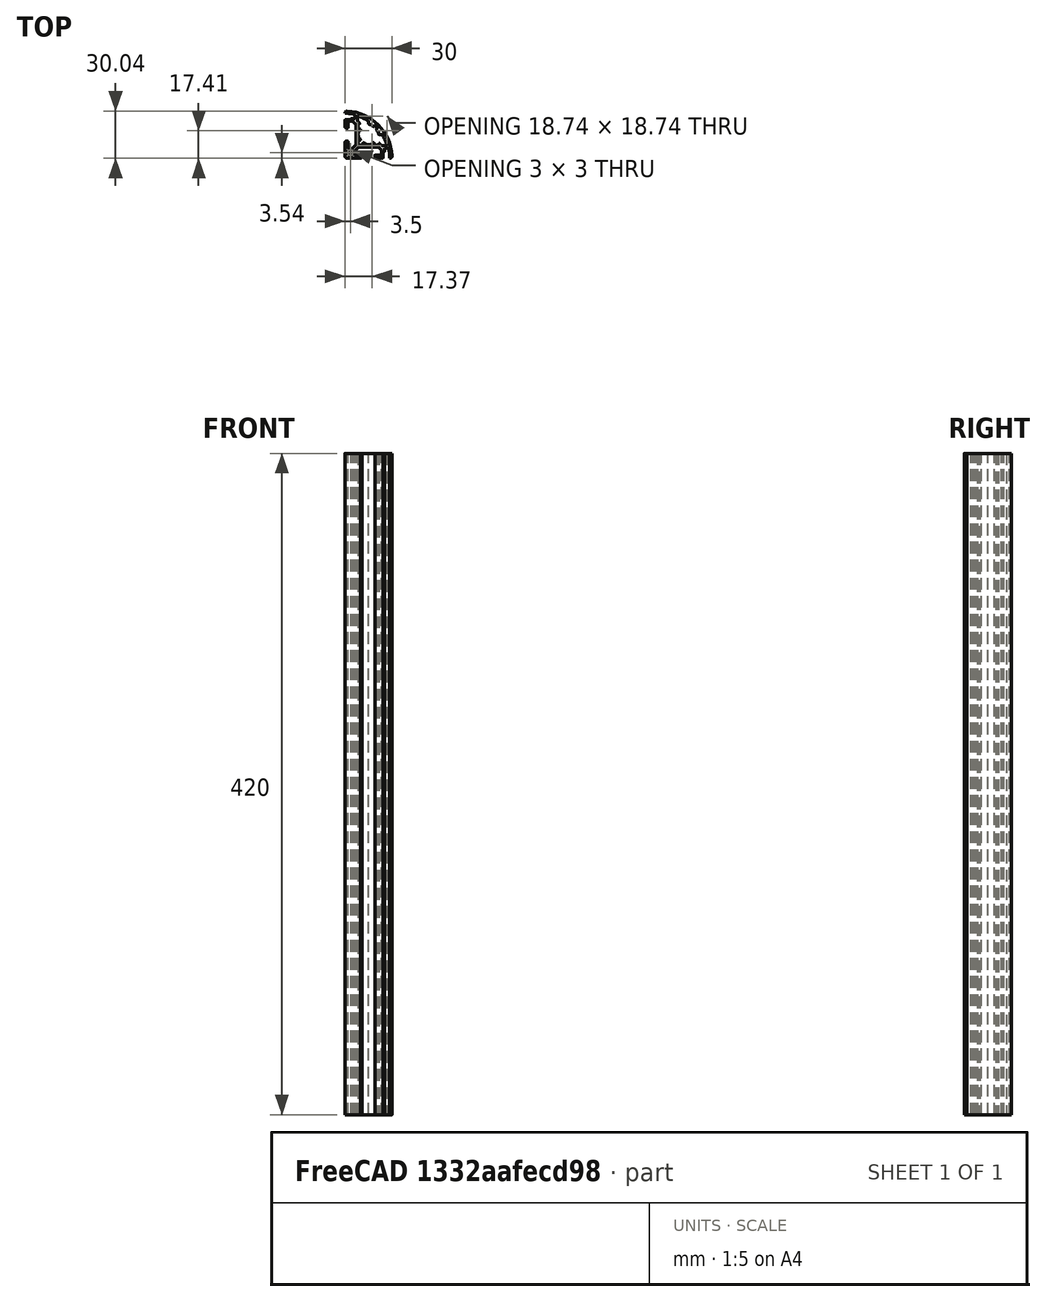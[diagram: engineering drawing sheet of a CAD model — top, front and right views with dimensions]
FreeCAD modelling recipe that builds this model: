
FCSTD DOCUMENT  (FreeCAD 0.17R13387 (Git))
Label: Z-Profile_3030_rounded_enclosure
License: All rights reserved
LicenseURL: http://en.wikipedia.org/wiki/All_rights_reserved
objects: Sketcher::SketchObject×1, PartDesign::Pad×1, PartDesign::Body×1
note: 4 computed .brp shape members not serialized (recipe doc carries the construction recipe); baked Part::Feature solids carry a one-line shape summary decoded from their .brp

FEATURE [Sketcher::SketchObject] Sketch155
  sketch-geometry (152):
    g0: ArcOfCircle CenterX=4.7 CenterY=4.69999 CenterZ=0 NormalX=0 NormalY=0 NormalZ=1 AngleXU=0 Radius=0.3 StartAngle=0 EndAngle=1.5708
    g1: ArcOfCircle CenterX=8.81823 CenterY=16.657 CenterZ=0 NormalX=0 NormalY=0 NormalZ=1 AngleXU=0 Radius=0.1 StartAngle=1.7017 EndAngle=2.8797
    g2: ArcOfCircle CenterX=15 CenterY=15 CenterZ=0 NormalX=0 NormalY=0 NormalZ=1 AngleXU=0 Radius=6.5 StartAngle=3.14159 EndAngle=3.40349
    g3: LineSegment StartX=8.80518 StartY=13.2438 StartZ=0 EndX=9.16477 EndY=13.1965 EndZ=0
    g4: ArcOfCircle CenterX=8.81823 CenterY=13.343 CenterZ=0 NormalX=0 NormalY=0 NormalZ=1 AngleXU=0 Radius=0.1 StartAngle=3.40349 EndAngle=4.58149
    g5: ArcOfCircle CenterX=15 CenterY=15 CenterZ=0 NormalX=0 NormalY=0 NormalZ=1 AngleXU=0 Radius=6.5 StartAngle=2.8797 EndAngle=3.14159
    g6: ArcOfCircle CenterX=9.15172 CenterY=13.0973 CenterZ=0 NormalX=0 NormalY=0 NormalZ=1 AngleXU=3.14159 Radius=0.1 StartAngle=3.45613 EndAngle=4.58149
    g7: ArcOfCircle CenterX=15 CenterY=15 CenterZ=0 NormalX=0 NormalY=0 NormalZ=1 AngleXU=0 Radius=6.05 StartAngle=3.45613 EndAngle=3.68754
    g8: ArcOfCircle CenterX=9.57305 CenterY=11.7029 CenterZ=0 NormalX=0 NormalY=0 NormalZ=1 AngleXU=3.14159 Radius=0.3 StartAngle=2.00713 EndAngle=3.68754
    g9: LineSegment StartX=9.69983 StartY=11.431 StartZ=0 EndX=8.60619 EndY=10.921 EndZ=0
    g10: ArcOfCircle CenterX=8.73298 CenterY=10.6492 CenterZ=0 NormalX=0 NormalY=0 NormalZ=1 AngleXU=0 Radius=0.3 StartAngle=2.00713 EndAngle=3.0624
    g11: LineSegment StartX=8.43392 StartY=10.6729 StartZ=0 EndX=8.28803 EndY=8.83442 EndZ=0
    g12: ArcOfCircle CenterX=8.78646 CenterY=8.79487 CenterZ=0 NormalX=0 NormalY=0 NormalZ=1 AngleXU=0 Radius=0.5 StartAngle=3.0624 EndAngle=4.8069
    g13: LineSegment StartX=8.83364 StartY=8.2971 StartZ=0 EndX=10.6958 EndY=8.47362 EndZ=0
    g14: ArcOfCircle CenterX=10.6675 CenterY=8.77228 CenterZ=0 NormalX=0 NormalY=0 NormalZ=1 AngleXU=0 Radius=0.3 StartAngle=4.8069 EndAngle=5.84685
    g15: LineSegment StartX=10.9394 StartY=8.6455 StartZ=0 EndX=11.431 EndY=9.69982 EndZ=0
    g16: ArcOfCircle CenterX=11.7029 CenterY=9.57303 CenterZ=0 NormalX=0 NormalY=0 NormalZ=1 AngleXU=3.14159 Radius=0.3 StartAngle=4.16645 EndAngle=5.84685
    g17: ArcOfCircle CenterX=15 CenterY=15 CenterZ=0 NormalX=0 NormalY=0 NormalZ=1 AngleXU=0 Radius=6.05 StartAngle=4.16645 EndAngle=4.39785
    g18: ArcOfCircle CenterX=13.0973 CenterY=9.15171 CenterZ=0 NormalX=0 NormalY=0 NormalZ=1 AngleXU=3.14159 Radius=0.1 StartAngle=3.27249 EndAngle=4.39785
    g19: LineSegment StartX=13.1965 StartY=9.16476 StartZ=0 EndX=13.2438 EndY=8.80517 EndZ=0
    g20: ArcOfCircle CenterX=13.343 CenterY=8.81822 CenterZ=0 NormalX=0 NormalY=0 NormalZ=1 AngleXU=0 Radius=0.1 StartAngle=3.27249 EndAngle=4.45049
    g21: ArcOfCircle CenterX=15 CenterY=15 CenterZ=0 NormalX=0 NormalY=0 NormalZ=1 AngleXU=0 Radius=6.5 StartAngle=4.45049 EndAngle=4.71239
    g22: ArcOfCircle CenterX=15 CenterY=15 CenterZ=0 NormalX=0 NormalY=0 NormalZ=1 AngleXU=0 Radius=6.5 StartAngle=4.71239 EndAngle=4.97428
    g23: ArcOfCircle CenterX=16.657 CenterY=8.81822 CenterZ=0 NormalX=0 NormalY=0 NormalZ=1 AngleXU=0 Radius=0.1 StartAngle=4.97428 EndAngle=6.15229
    g24: LineSegment StartX=16.7562 StartY=8.80517 StartZ=0 EndX=16.8035 EndY=9.16476 EndZ=0
    g25: ArcOfCircle CenterX=16.9027 CenterY=9.15171 CenterZ=0 NormalX=0 NormalY=0 NormalZ=1 AngleXU=3.14159 Radius=0.1 StartAngle=5.02693 EndAngle=6.15229
    g26: ArcOfCircle CenterX=15 CenterY=15 CenterZ=0 NormalX=0 NormalY=0 NormalZ=1 AngleXU=0 Radius=6.05 StartAngle=5.02693 EndAngle=5.25833
    g27: ArcOfCircle CenterX=18.2971 CenterY=9.57303 CenterZ=0 NormalX=0 NormalY=0 NormalZ=1 AngleXU=3.14159 Radius=0.3 StartAngle=3.57792 EndAngle=5.25833
    g28: LineSegment StartX=18.569 StartY=9.69982 StartZ=0 EndX=19.0789 EndY=8.60618 EndZ=0
    g29: ArcOfCircle CenterX=19.3508 CenterY=8.73297 CenterZ=0 NormalX=0 NormalY=0 NormalZ=1 AngleXU=0 Radius=0.3 StartAngle=3.57792 EndAngle=4.6332
    g30: LineSegment StartX=19.3271 StartY=8.43391 StartZ=0 EndX=21.1656 EndY=8.28801 EndZ=0
    g31: ArcOfCircle CenterX=21.2051 CenterY=8.78645 CenterZ=0 NormalX=0 NormalY=0 NormalZ=1 AngleXU=0 Radius=0.5 StartAngle=4.6332 EndAngle=6.3777
    g32: LineSegment StartX=21.7029 StartY=8.83363 StartZ=0 EndX=21.6748 EndY=9.12955 EndZ=0
    g33: ArcOfCircle CenterX=21.9735 CenterY=9.15786 CenterZ=0 NormalX=0 NormalY=0 NormalZ=1 AngleXU=3.14159 Radius=0.3 StartAngle=3.92699 EndAngle=6.3777
    g34: LineSegment StartX=22.1856 StartY=9.36999 StartZ=0 EndX=23.4678 EndY=8.08785 EndZ=0
    g35: ArcOfCircle CenterX=23.6799 CenterY=8.29999 CenterZ=0 NormalX=0 NormalY=0 NormalZ=1 AngleXU=0 Radius=0.3 StartAngle=3.92699 EndAngle=4.71239
    g36: LineSegment StartX=23.6799 StartY=7.99999 StartZ=0 EndX=26.4413 EndY=7.99999 EndZ=0
    g37: ArcOfCircle CenterX=26.4413 CenterY=8.29999 CenterZ=0 NormalX=0 NormalY=0 NormalZ=1 AngleXU=0 Radius=0.3 StartAngle=4.71239 EndAngle=6.59012
    g38: ArcOfCircle CenterX=-0.118084 CenterY=-0.118082 CenterZ=0 NormalX=0 NormalY=0 NormalZ=1 AngleXU=0 Radius=28.1615 StartAngle=0.306936 EndAngle=0.56078
    g39: ArcOfCircle CenterX=23.4762 CenterY=14.7 CenterZ=0 NormalX=0 NormalY=0 NormalZ=1 AngleXU=0 Radius=0.3 StartAngle=0.560781 EndAngle=1.5708
    g40: LineSegment StartX=23.4762 StartY=15 StartZ=0 EndX=21.7934 EndY=15 EndZ=0
    g41: ArcOfCircle CenterX=21.7934 CenterY=15.3 CenterZ=0 NormalX=0 NormalY=0 NormalZ=1 AngleXU=3.14159 Radius=0.3 StartAngle=0.044132 EndAngle=1.5708
    g42: ArcOfCircle CenterX=15 CenterY=15 CenterZ=0 NormalX=0 NormalY=0 NormalZ=1 AngleXU=0 Radius=6.5 StartAngle=0.044132 EndAngle=0.261895
    g43: ArcOfCircle CenterX=21.1818 CenterY=16.657 CenterZ=0 NormalX=0 NormalY=0 NormalZ=1 AngleXU=0 Radius=0.1 StartAngle=0.261895 EndAngle=1.4399
    g44: LineSegment StartX=21.1948 StartY=16.7562 StartZ=0 EndX=20.8352 EndY=16.8035 EndZ=0
    g45: ArcOfCircle CenterX=20.8483 CenterY=16.9026 CenterZ=0 NormalX=0 NormalY=0 NormalZ=1 AngleXU=3.14159 Radius=0.1 StartAngle=0.314537 EndAngle=1.4399
    g46: ArcOfCircle CenterX=15 CenterY=15 CenterZ=0 NormalX=0 NormalY=0 NormalZ=1 AngleXU=0 Radius=6.05 StartAngle=0.314537 EndAngle=0.545943
    g47: ArcOfCircle CenterX=20.427 CenterY=18.2971 CenterZ=0 NormalX=0 NormalY=0 NormalZ=1 AngleXU=3.14159 Radius=0.3 StartAngle=5.14872 EndAngle=6.82913
    g48: LineSegment StartX=20.3002 StartY=18.569 StartZ=0 EndX=20.3872 EndY=18.6095 EndZ=0
    g49: ArcOfCircle CenterX=20.2604 CenterY=18.8814 CenterZ=0 NormalX=0 NormalY=0 NormalZ=1 AngleXU=0 Radius=0.3 StartAngle=5.14872 EndAngle=7.03358
    g50: ArcOfCircle CenterX=-0.118084 CenterY=-0.118096 CenterZ=0 NormalX=0 NormalY=0 NormalZ=1 AngleXU=0 Radius=28.1615 StartAngle=0.750394 EndAngle=0.820403
    g51: ArcOfCircle CenterX=18.8814 CenterY=20.2604 CenterZ=0 NormalX=0 NormalY=0 NormalZ=1 AngleXU=0 Radius=0.3 StartAngle=0.820403 EndAngle=2.70526
    g52: LineSegment StartX=18.6095 StartY=20.3872 StartZ=0 EndX=18.569 EndY=20.3002 EndZ=0
    g53: ArcOfCircle CenterX=18.2971 CenterY=20.4269 CenterZ=0 NormalX=0 NormalY=0 NormalZ=1 AngleXU=3.14159 Radius=0.3 StartAngle=1.02485 EndAngle=2.70526
    g54: ArcOfCircle CenterX=15 CenterY=15 CenterZ=0 NormalX=0 NormalY=0 NormalZ=1 AngleXU=0 Radius=6.05 StartAngle=1.02485 EndAngle=1.25626
    g55: ArcOfCircle CenterX=16.9027 CenterY=20.8483 CenterZ=0 NormalX=0 NormalY=0 NormalZ=1 AngleXU=3.14159 Radius=0.1 StartAngle=0.1309 EndAngle=1.25626
    g56: LineSegment StartX=16.8035 StartY=20.8352 StartZ=0 EndX=16.7562 EndY=21.1948 EndZ=0
    g57: ArcOfCircle CenterX=16.657 CenterY=21.1818 CenterZ=0 NormalX=0 NormalY=0 NormalZ=1 AngleXU=0 Radius=0.1 StartAngle=0.1309 EndAngle=1.3089
    g58: ArcOfCircle CenterX=15 CenterY=15 CenterZ=0 NormalX=0 NormalY=0 NormalZ=1 AngleXU=0 Radius=6.5 StartAngle=1.3089 EndAngle=1.52666
    g59: ArcOfCircle CenterX=15.3 CenterY=21.7934 CenterZ=0 NormalX=0 NormalY=0 NormalZ=1 AngleXU=3.14159 Radius=0.3 StartAngle=0 EndAngle=1.52666
    g60: LineSegment StartX=15 StartY=21.7934 StartZ=0 EndX=15 EndY=23.4762 EndZ=0
    g61: ArcOfCircle CenterX=14.7 CenterY=23.4762 CenterZ=0 NormalX=0 NormalY=0 NormalZ=1 AngleXU=0 Radius=0.3 StartAngle=0 EndAngle=1.01002
    g62: ArcOfCircle CenterX=-0.118084 CenterY=-0.118096 CenterZ=0 NormalX=0 NormalY=0 NormalZ=1 AngleXU=0 Radius=28.1615 StartAngle=1.01002 EndAngle=1.26386
    g63: ArcOfCircle CenterX=8.3 CenterY=26.4413 CenterZ=0 NormalX=0 NormalY=0 NormalZ=1 AngleXU=0 Radius=0.3 StartAngle=1.26386 EndAngle=3.14159
    g64: LineSegment StartX=8 StartY=26.4413 StartZ=0 EndX=8 EndY=23.6799 EndZ=0
    g65: ArcOfCircle CenterX=8.3 CenterY=23.6799 CenterZ=0 NormalX=0 NormalY=0 NormalZ=1 AngleXU=0 Radius=0.3 StartAngle=3.14159 EndAngle=3.92699
    g66: LineSegment StartX=8.08787 StartY=23.4678 StartZ=0 EndX=9.37 EndY=22.1856 EndZ=0
    g67: ArcOfCircle CenterX=9.15787 CenterY=21.9735 CenterZ=0 NormalX=0 NormalY=0 NormalZ=1 AngleXU=3.14159 Radius=0.3 StartAngle=1.47628 EndAngle=3.92699
    g68: LineSegment StartX=9.12956 StartY=21.6748 StartZ=0 EndX=8.83364 EndY=21.7029 EndZ=0
    g69: ArcOfCircle CenterX=8.78646 CenterY=21.2051 CenterZ=0 NormalX=0 NormalY=0 NormalZ=1 AngleXU=0 Radius=0.5 StartAngle=1.47628 EndAngle=3.22078
    g70: LineSegment StartX=8.28803 StartY=21.1656 StartZ=0 EndX=8.43392 EndY=19.3271 EndZ=0
    g71: ArcOfCircle CenterX=8.73298 CenterY=19.3508 CenterZ=0 NormalX=0 NormalY=0 NormalZ=1 AngleXU=0 Radius=0.3 StartAngle=3.22078 EndAngle=4.27606
    g72: LineSegment StartX=8.60619 StartY=19.0789 StartZ=0 EndX=9.69983 EndY=18.569 EndZ=0
    g73: ArcOfCircle CenterX=9.57305 CenterY=18.2971 CenterZ=0 NormalX=0 NormalY=0 NormalZ=1 AngleXU=3.14159 Radius=0.3 StartAngle=2.59565 EndAngle=4.27606
    g74: ArcOfCircle CenterX=24.7 CenterY=3.69999 CenterZ=0 NormalX=0 NormalY=0 NormalZ=1 AngleXU=3.14159 Radius=0.3 StartAngle=4.71239 EndAngle=6.28319
    g75: ArcOfCircle CenterX=15 CenterY=15 CenterZ=0 NormalX=0 NormalY=0 NormalZ=1 AngleXU=0 Radius=6.05 StartAngle=2.59565 EndAngle=2.82706
    g76: ArcOfCircle CenterX=9.15172 CenterY=16.9026 CenterZ=0 NormalX=0 NormalY=0 NormalZ=1 AngleXU=3.14159 Radius=0.1 StartAngle=1.7017 EndAngle=2.82706
    g77: LineSegment StartX=9.16477 StartY=16.8035 StartZ=0 EndX=8.80518 EndY=16.7562 EndZ=0
    g78: ArcOfCircle CenterX=21.2201 CenterY=6.79999 CenterZ=0 NormalX=0 NormalY=0 NormalZ=1 AngleXU=3.14159 Radius=0.300013 StartAngle=3.92699 EndAngle=4.71239
    g79: LineSegment StartX=21.4322 StartY=7.01213 StartZ=0 EndX=23.3121 EndY=5.13222 EndZ=0
    g80: ArcOfCircle CenterX=23.1 CenterY=4.92009 CenterZ=0 NormalX=0 NormalY=0 NormalZ=1 AngleXU=3.14159 Radius=0.3 StartAngle=3.14159 EndAngle=3.92699
    g81: LineSegment StartX=23.4 StartY=4.92009 StartZ=0 EndX=23.4 EndY=2.29999 EndZ=0
    g82: ArcOfCircle CenterX=23.1 CenterY=2.29999 CenterZ=0 NormalX=0 NormalY=0 NormalZ=1 AngleXU=3.14159 Radius=0.3 StartAngle=1.5708 EndAngle=3.14159
    g83: LineSegment StartX=23.1 StartY=1.99999 StartZ=0 EndX=19.25 EndY=1.99999 EndZ=0
    g84: ArcOfCircle CenterX=19.25 CenterY=1.89999 CenterZ=0 NormalX=0 NormalY=0 NormalZ=1 AngleXU=0 Radius=0.1 StartAngle=1.5708 EndAngle=3.14159
    g85: LineSegment StartX=19.15 StartY=1.89999 StartZ=0 EndX=19.15 EndY=0.999987 EndZ=0
    g86: LineSegment StartX=24.7 StartY=3.99999 StartZ=0 EndX=24.846 EndY=3.99999 EndZ=0
    g87: ArcOfCircle CenterX=24.846 CenterY=4.29999 CenterZ=0 NormalX=0 NormalY=0 NormalZ=1 AngleXU=0 Radius=0.3 StartAngle=4.71239 EndAngle=6.28319
    g88: LineSegment StartX=25.146 StartY=4.29999 StartZ=0 EndX=25.146 EndY=6.19999 EndZ=0
    g89: ArcOfCircle CenterX=25.446 CenterY=6.19999 CenterZ=0 NormalX=0 NormalY=0 NormalZ=1 AngleXU=3.14159 Radius=0.299924 StartAngle=4.71239 EndAngle=6.28319
    g90: LineSegment StartX=25.446 StartY=6.49991 StartZ=0 EndX=27.5299 EndY=6.49991 EndZ=0
    g91: ArcOfCircle CenterX=27.5299 CenterY=6.19999 CenterZ=0 NormalX=0 NormalY=0 NormalZ=1 AngleXU=3.14159 Radius=0.299923 StartAngle=3.36625 EndAngle=4.71239
    g92: ArcOfCircle CenterX=-0.118084 CenterY=-0.118096 CenterZ=0 NormalX=0 NormalY=0 NormalZ=1 AngleXU=3.14159 Radius=28.6606 StartAngle=3.19665 EndAngle=3.36625
    g93: ArcOfCircle CenterX=1.5 CenterY=28.5 CenterZ=0 NormalX=0 NormalY=0 NormalZ=1 AngleXU=0 Radius=1.5 StartAngle=1.57078 EndAngle=3.14159
    g94: LineSegment StartX=-4.21128e-07 StartY=28.5 StartZ=0 EndX=1.45922 EndY=28.5 EndZ=0
    g95: ArcOfCircle CenterX=-0.118084 CenterY=-0.118096 CenterZ=0 NormalX=0 NormalY=0 NormalZ=1 AngleXU=3.14159 Radius=28.6615 StartAngle=4.48773 EndAngle=4.65733
    g96: ArcOfCircle CenterX=6.2 CenterY=27.5307 CenterZ=0 NormalX=0 NormalY=0 NormalZ=1 AngleXU=3.14159 Radius=0.3 StartAngle=3.14159 EndAngle=4.48773
    g97: LineSegment StartX=6.5 StartY=27.5307 StartZ=0 EndX=6.5 EndY=25.446 EndZ=0
    g98: ArcOfCircle CenterX=6.2 CenterY=25.446 CenterZ=0 NormalX=0 NormalY=0 NormalZ=1 AngleXU=3.14159 Radius=0.3 StartAngle=1.5708 EndAngle=3.14159
    g99: ArcOfCircle CenterX=4.3201 CenterY=6.29999 CenterZ=0 NormalX=0 NormalY=0 NormalZ=1 AngleXU=3.14159 Radius=0.3 StartAngle=1.5708 EndAngle=2.35619
    g100: LineSegment StartX=6.2 StartY=25.146 StartZ=0 EndX=4.3 EndY=25.146 EndZ=0
    g101: ArcOfCircle CenterX=4.3 CenterY=24.846 CenterZ=0 NormalX=0 NormalY=0 NormalZ=1 AngleXU=0 Radius=0.3 StartAngle=1.5708 EndAngle=3.14159
    g102: LineSegment StartX=4 StartY=24.846 StartZ=0 EndX=4 EndY=24.7 EndZ=0
    g103: ArcOfCircle CenterX=3.7 CenterY=24.7 CenterZ=0 NormalX=0 NormalY=0 NormalZ=1 AngleXU=3.14159 Radius=0.3 StartAngle=1.5708 EndAngle=3.14159
    g104: LineSegment StartX=3.7 StartY=24.4 StartZ=0 EndX=0.5 EndY=24.4 EndZ=0
    g105: ArcOfCircle CenterX=0.5 CenterY=23.9 CenterZ=0 NormalX=0 NormalY=0 NormalZ=1 AngleXU=0 Radius=0.5 StartAngle=1.5708 EndAngle=3.14159
    g106: LineSegment StartX=-4.21297e-07 StartY=23.9 StartZ=0 EndX=-4.21297e-07 EndY=20.15 EndZ=0
    g107: ArcOfCircle CenterX=1 CenterY=20.15 CenterZ=0 NormalX=0 NormalY=0 NormalZ=1 AngleXU=0 Radius=1 StartAngle=3.14159 EndAngle=4.71239
    g108: LineSegment StartX=1 StartY=19.15 StartZ=0 EndX=1.9 EndY=19.15 EndZ=0
    g109: ArcOfCircle CenterX=1.9 CenterY=19.25 CenterZ=0 NormalX=0 NormalY=0 NormalZ=1 AngleXU=0 Radius=0.1 StartAngle=4.71239 EndAngle=6.28319
    g110: LineSegment StartX=2 StartY=19.25 StartZ=0 EndX=2 EndY=23.1 EndZ=0
    g111: ArcOfCircle CenterX=2.3 CenterY=23.1 CenterZ=0 NormalX=0 NormalY=0 NormalZ=1 AngleXU=3.14159 Radius=0.3 StartAngle=4.71239 EndAngle=6.28319
    g112: LineSegment StartX=2.3 StartY=23.4 StartZ=0 EndX=4.9201 EndY=23.4 EndZ=0
    g113: ArcOfCircle CenterX=4.9201 CenterY=23.1 CenterZ=0 NormalX=0 NormalY=0 NormalZ=1 AngleXU=3.14159 Radius=0.3 StartAngle=3.92699 EndAngle=4.71239
    g114: LineSegment StartX=5.13223 StartY=23.3121 StartZ=0 EndX=7.01213 EndY=21.4321 EndZ=0
    g115: ArcOfCircle CenterX=6.8 CenterY=21.22 CenterZ=0 NormalX=0 NormalY=0 NormalZ=1 AngleXU=3.14159 Radius=0.3 StartAngle=3.14159 EndAngle=3.92699
    g116: ArcOfCircle CenterX=6.8 CenterY=8.78 CenterZ=0 NormalX=0 NormalY=0 NormalZ=1 AngleXU=3.14159 Radius=0.3 StartAngle=2.35619 EndAngle=3.14159
    g117: LineSegment StartX=7.01213 StartY=8.56787 StartZ=0 EndX=4.53223 EndY=6.08785 EndZ=0
    g118: LineSegment StartX=2 StartY=4.69999 StartZ=0 EndX=2 EndY=2.29999 EndZ=0
    g119: LineSegment StartX=4.3201 StartY=5.99999 StartZ=0 EndX=2.3 EndY=5.99999 EndZ=0
    g120: ArcOfCircle CenterX=2.3 CenterY=6.29999 CenterZ=0 NormalX=0 NormalY=0 NormalZ=1 AngleXU=3.14159 Radius=0.3 StartAngle=0 EndAngle=1.5708
    g121: LineSegment StartX=2 StartY=6.29999 StartZ=0 EndX=2 EndY=10.75 EndZ=0
    g122: ArcOfCircle CenterX=1.9 CenterY=10.75 CenterZ=0 NormalX=0 NormalY=0 NormalZ=1 AngleXU=0 Radius=0.1 StartAngle=0 EndAngle=1.5708
    g123: LineSegment StartX=1.9 StartY=10.85 StartZ=0 EndX=1.00001 EndY=10.85 EndZ=0
    g124: ArcOfCircle CenterX=1.00001 CenterY=9.84999 CenterZ=0 NormalX=0 NormalY=0 NormalZ=1 AngleXU=0 Radius=1 StartAngle=1.5708 EndAngle=3.14159
    g125: LineSegment StartX=6.10972e-06 StartY=9.84999 StartZ=0 EndX=6.10972e-06 EndY=1.49999 EndZ=0
    g126: LineSegment StartX=10.8523 StartY=1.00012 StartZ=0 EndX=10.8523 EndY=1.89765 EndZ=0
    g127: ArcOfCircle CenterX=10.75 CenterY=1.89765 CenterZ=0 NormalX=0 NormalY=0 NormalZ=1 AngleXU=0 Radius=0.102333 StartAngle=0 EndAngle=1.5708
    g128: LineSegment StartX=10.75 StartY=1.99999 StartZ=0 EndX=6.3 EndY=1.99999 EndZ=0
    g129: ArcOfCircle CenterX=6.3 CenterY=2.29999 CenterZ=0 NormalX=0 NormalY=0 NormalZ=1 AngleXU=3.14159 Radius=0.3 StartAngle=0 EndAngle=1.5708
    g130: LineSegment StartX=6 StartY=2.29999 StartZ=0 EndX=6 EndY=4.32009 EndZ=0
    g131: ArcOfCircle CenterX=6.3 CenterY=4.32009 CenterZ=0 NormalX=0 NormalY=0 NormalZ=1 AngleXU=3.14159 Radius=0.3 StartAngle=5.49779 EndAngle=6.28319
    g132: LineSegment StartX=6.08787 StartY=4.53222 StartZ=0 EndX=8.5678 EndY=7.01213 EndZ=0
    g133: ArcOfCircle CenterX=8.77995 CenterY=6.79999 CenterZ=0 NormalX=0 NormalY=0 NormalZ=1 AngleXU=3.14159 Radius=0.300012 StartAngle=4.71239 EndAngle=5.49779
    g134: LineSegment StartX=4.7 StartY=4.99999 StartZ=0 EndX=2.3 EndY=4.99999 EndZ=0
    g135: ArcOfCircle CenterX=2.3 CenterY=4.69999 CenterZ=0 NormalX=0 NormalY=0 NormalZ=1 AngleXU=0 Radius=0.3 StartAngle=1.5708 EndAngle=3.14159
    g136: ArcOfCircle CenterX=2.3 CenterY=2.29999 CenterZ=0 NormalX=0 NormalY=0 NormalZ=1 AngleXU=0 Radius=0.3 StartAngle=3.14159 EndAngle=4.71239
    g137: LineSegment StartX=2.3 StartY=1.99999 StartZ=0 EndX=4.7 EndY=1.99999 EndZ=0
    g138: ArcOfCircle CenterX=4.7 CenterY=2.29999 CenterZ=0 NormalX=0 NormalY=0 NormalZ=1 AngleXU=0 Radius=0.3 StartAngle=4.71239 EndAngle=6.28319
    g139: LineSegment StartX=5 StartY=2.29999 StartZ=0 EndX=5 EndY=4.69999 EndZ=0
    g140: ArcOfCircle CenterX=-0.118084 CenterY=-0.116576 CenterZ=0 NormalX=0 NormalY=0 NormalZ=1 AngleXU=0 Radius=30.16 StartAngle=0.0536253 EndAngle=1.51712
    g141: LineSegment StartX=8.77995 StartY=7.1 StartZ=0 EndX=21.2201 EndY=7.1 EndZ=0
    g142: LineSegment StartX=7.1 StartY=21.22 StartZ=0 EndX=7.1 EndY=8.78 EndZ=0
    g143: LineSegment StartX=24.4 StartY=0.499987 StartZ=0 EndX=24.4 EndY=3.69999 EndZ=0
    g144: LineSegment StartX=28.4991 StartY=1.45921 StartZ=0 EndX=28.4991 EndY=-0.0407918 EndZ=0
    g145: ArcOfCircle CenterX=20.15 CenterY=0.999987 CenterZ=0 NormalX=0 NormalY=0 NormalZ=1 AngleXU=0 Radius=1 StartAngle=3.14159 EndAngle=4.71239
    g146: LineSegment StartX=20.15 StartY=-1.30622e-05 StartZ=0 EndX=23.9 EndY=-1.30622e-05 EndZ=0
    g147: ArcOfCircle CenterX=23.9 CenterY=0.499987 CenterZ=0 NormalX=0 NormalY=0 NormalZ=1 AngleXU=0 Radius=0.5 StartAngle=4.71239 EndAngle=6.28319
    g148: ArcOfCircle CenterX=28.4991 CenterY=1.45921 CenterZ=0 NormalX=0 NormalY=0 NormalZ=1 AngleXU=0 Radius=1.5 StartAngle=4.71239 EndAngle=6.31037
    g149: ArcOfCircle CenterX=1.50001 CenterY=1.49999 CenterZ=0 NormalX=0 NormalY=0 NormalZ=1 AngleXU=0 Radius=1.5 StartAngle=3.1416 EndAngle=4.71238
    g150: LineSegment StartX=1.5 StartY=-7.06199e-06 StartZ=0 EndX=9.85 EndY=-7.06199e-06 EndZ=0
    g151: ArcOfCircle CenterX=9.90533 CenterY=0.946878 CenterZ=0 NormalX=0 NormalY=0 NormalZ=1 AngleXU=0 Radius=0.9485 StartAngle=4.65402 EndAngle=6.33935
  constraints (208):
    c: Coincident(g0,g139)
    c: Coincident(g0,g134)
    c: Coincident(g134,g135)
    c: Coincident(g118,g135)
    c: Coincident(g118,g136)
    c: Coincident(g136,g137)
    c: Coincident(g137,g138)
    c: Coincident(g138,g139)
    c: Coincident(g131,g132)
    c: Coincident(g130,g131)
    c: Coincident(g129,g130)
    c: Coincident(g128,g129)
    c: Coincident(g127,g128)
    c: Coincident(g126,g127)
    c: Coincident(g126,g151)
    c: Coincident(g150,g151)
    c: Coincident(g149,g150)
    c: Coincident(g125,g149)
    c: Coincident(g124,g125)
    c: Coincident(g123,g124)
    c: Coincident(g122,g123)
    c: Coincident(g121,g122)
    c: Coincident(g120,g121)
    c: Coincident(g119,g120)
    c: Coincident(g99,g119)
    c: Coincident(g99,g117)
    c: Coincident(g116,g117)
    c: Coincident(g116,g142)
    c: Coincident(g115,g142)
    c: Coincident(g114,g115)
    c: Coincident(g113,g114)
    c: Coincident(g112,g113)
    c: Coincident(g111,g112)
    c: Coincident(g110,g111)
    c: Coincident(g109,g110)
    c: Coincident(g108,g109)
    c: Coincident(g107,g108)
    c: Coincident(g106,g107)
    c: Coincident(g105,g106)
    c: Coincident(g104,g105)
    c: Coincident(g103,g104)
    c: Coincident(g102,g103)
    c: Coincident(g101,g102)
    c: Coincident(g100,g101)
    c: Coincident(g98,g100)
    c: Coincident(g97,g98)
    c: Coincident(g96,g97)
    c: Coincident(g95,g96)
    c: Coincident(g94,g95)
    c: Coincident(g93,g94)
    c: Coincident(g93,g140)
    c: Coincident(g140,g148)
    c: Coincident(g144,g148)
    c: Coincident(g92,g144)
    c: Coincident(g92,g148)
    c: Coincident(g91,g92)
    c: Coincident(g90,g91)
    c: Coincident(g89,g90)
    c: Coincident(g88,g89)
    c: Coincident(g87,g88)
    c: Coincident(g86,g87)
    c: Coincident(g74,g86)
    c: Coincident(g74,g143)
    c: Coincident(g143,g147)
    c: Coincident(g146,g147)
    c: Coincident(g145,g146)
    c: Coincident(g85,g145)
    c: Coincident(g84,g85)
    c: Coincident(g83,g84)
    c: Coincident(g82,g83)
    c: Coincident(g81,g82)
    c: Coincident(g80,g81)
    c: Coincident(g79,g80)
    c: Coincident(g78,g79)
    c: Coincident(g78,g141)
    c: Coincident(g133,g141)
    c: Coincident(g132,g133)
    c: Coincident(g12,g13)
    c: Coincident(g13,g14)
    c: Coincident(g14,g15)
    c: Coincident(g15,g16)
    c: Coincident(g16,g17)
    c: Coincident(g17,g18)
    c: Coincident(g18,g19)
    c: Coincident(g19,g20)
    c: Coincident(g20,g21)
    c: Coincident(g21,g22)
    c: Coincident(g22,g23)
    c: Coincident(g23,g24)
    c: Coincident(g24,g25)
    c: Coincident(g25,g26)
    c: Coincident(g26,g27)
    c: Coincident(g27,g28)
    c: Coincident(g28,g29)
    c: Coincident(g29,g30)
    c: Coincident(g30,g31)
    c: Coincident(g31,g32)
    c: Coincident(g32,g33)
    c: Coincident(g33,g34)
    c: Coincident(g34,g35)
    c: Coincident(g35,g36)
    c: Coincident(g36,g37)
    c: Coincident(g37,g38)
    c: Coincident(g38,g39)
    c: Coincident(g39,g40)
    c: Coincident(g40,g41)
    c: Coincident(g41,g42)
    c: Coincident(g42,g43)
    c: Coincident(g43,g44)
    c: Coincident(g44,g45)
    c: Coincident(g45,g46)
    c: Coincident(g46,g47)
    c: Coincident(g47,g48)
    c: Coincident(g48,g49)
    c: Coincident(g49,g50)
    c: Coincident(g50,g51)
    c: Coincident(g51,g52)
    c: Coincident(g52,g53)
    c: Coincident(g53,g54)
    c: Coincident(g54,g55)
    c: Coincident(g55,g56)
    c: Coincident(g56,g57)
    c: Coincident(g57,g58)
    c: Coincident(g58,g59)
    c: Coincident(g59,g60)
    c: Coincident(g60,g61)
    c: Coincident(g61,g62)
    c: Coincident(g62,g63)
    c: Coincident(g63,g64)
    c: Coincident(g64,g65)
    c: Coincident(g65,g66)
    c: Coincident(g66,g67)
    c: Coincident(g67,g68)
    c: Coincident(g68,g69)
    c: Coincident(g69,g70)
    c: Coincident(g70,g71)
    c: Coincident(g71,g72)
    c: Coincident(g72,g73)
    c: Coincident(g73,g75)
    c: Coincident(g75,g76)
    c: Coincident(g76,g77)
    c: Coincident(g1,g77)
    c: Coincident(g1,g5)
    c: Coincident(g2,g5)
    c: Coincident(g2,g4)
    c: Coincident(g3,g4)
    c: Coincident(g3,g6)
    c: Coincident(g6,g7)
    c: Coincident(g7,g8)
    c: Coincident(g8,g9)
    c: Coincident(g9,g10)
    c: Coincident(g10,g11)
    c: Coincident(g11,g12)
    c: Vertical(g64)
    c: Vertical(g97)
    c: Vertical(g106)
    c: Vertical(g110)
    c: Vertical(g142)
    c: Vertical(g121)
    c: Vertical(g125)
    c: Vertical(g118)
    c: Vertical(g139)
    c: Vertical(g130)
    c: Vertical(g81)
    c: Vertical(g143)
    c: Horizontal(g94)
    c: Horizontal(g104)
    c: Horizontal(g112)
    c: Horizontal(g108)
    c: Horizontal(g123)
    c: Horizontal(g119)
    c: Horizontal(g134)
    c: Horizontal(g137)
    c: Horizontal(g150)
    c: Horizontal(g128)
    c: Horizontal(g141)
    c: Horizontal(g83)
    c: Horizontal(g146)
    c: Horizontal(g90)
    c: Horizontal(g36)
    c: Horizontal(g40)
    c: Vertical(g126)
    c: Vertical(g85)
    c: Vertical(g60)
    c: Vertical(g144)
    c: Vertical(g88)
    c: Horizontal(g100)
    c: Coincident(g2,g5)
    c: Coincident(g2,g7)
    c: Coincident(g2,g17)
    c: Coincident(g2,g21)
    c: Coincident(g2,g22)
    c: Coincident(g2,g26)
    c: Coincident(g2,g42)
    c: Coincident(g2,g46)
    c: Coincident(g2,g54)
    c: Coincident(g2,g58)
    c: Coincident(g2,g75)
    c: DistanceX(g2) = 15
    c: DistanceY(g2) = 15
    c: Radius(g93) = 1.5
    c: Radius(g140) = 30.16
    c: Equal(g93,g148)
    c: Radius(g149) = 1.5
    c: DistanceY(g116) = 8.78
    c: DistanceY(g142,g142) = 12.44
    c: DistanceX(g116) = 7.1
    c: DistanceY(g133) = 7.1
FEATURE [PartDesign::Pad] Pad
  Length = 420
  Length2 = 100
  Profile = -> Sketch155
  Type = 0
FEATURE [PartDesign::Body] Body
  Group = -> [Sketch155,Pad]
  Origin = -> Origin
  Tip = -> Pad
